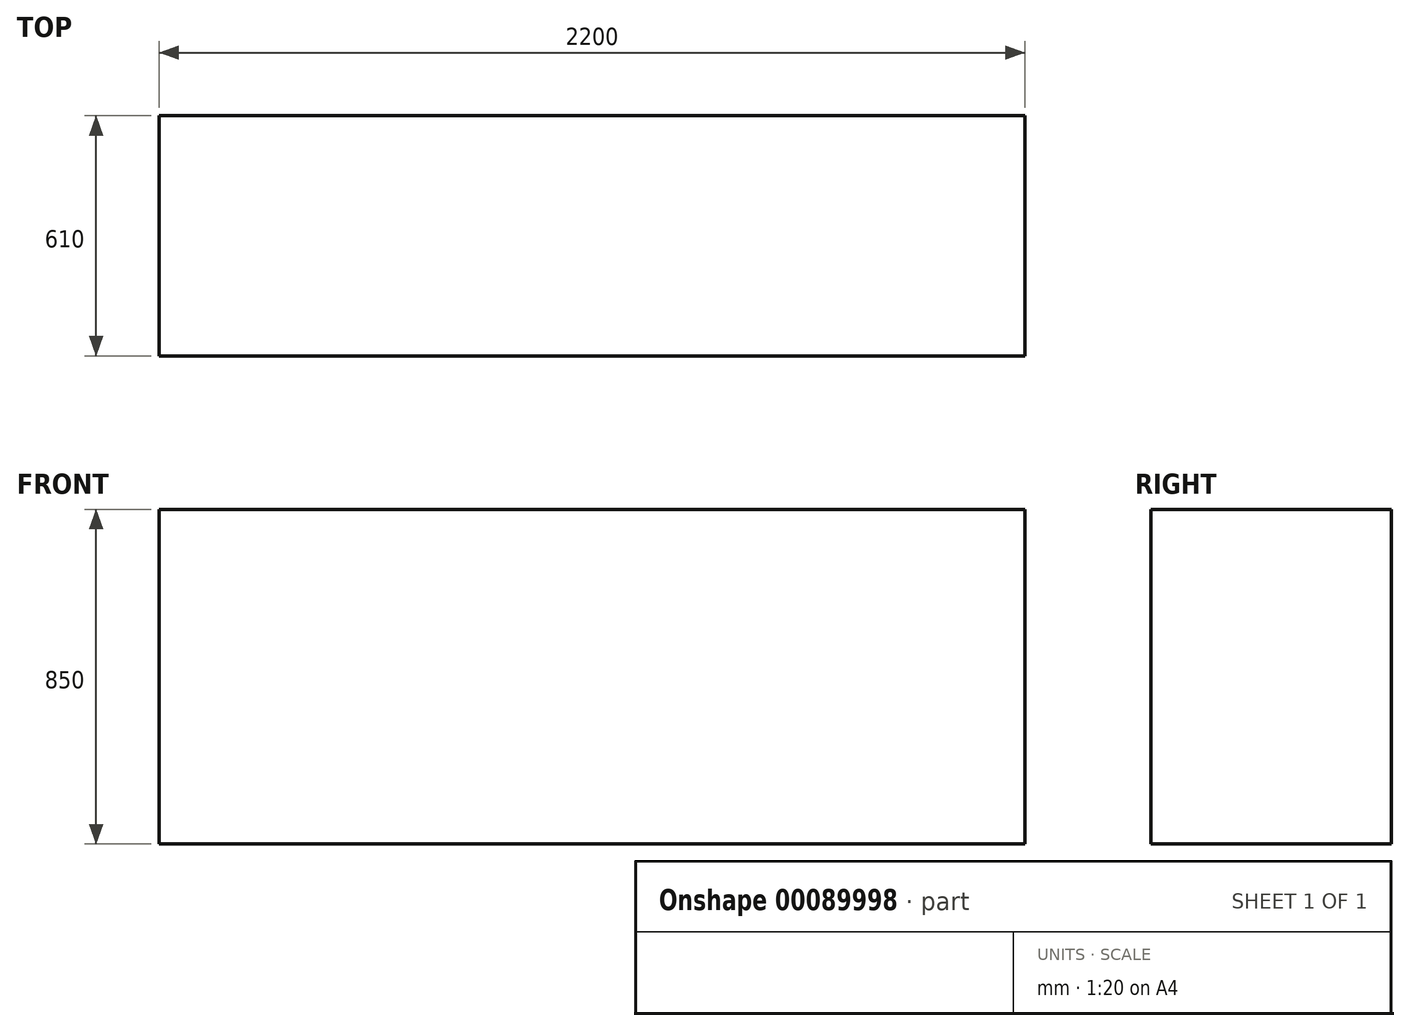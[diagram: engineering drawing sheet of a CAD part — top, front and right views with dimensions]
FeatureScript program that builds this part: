
annotation { "Feature Type Name" : "Feature", "Feature Type Description" : "" }
export const myFeature = defineFeature(function(context is Context, id is Id, definition is map)
    precondition{}
    {
        {
            var Q0;
            Q0=qCreatedBy(makeId("Top.planeOp"),FACE);
            var sketch = newSketch(context, id + "F0", { "sketchPlane" : qUnion([Q0])});
            skLineSegment(sketch, "E0.bottom", {"start": v(0, 0) * mm, "end": v(2200, 0) * mm});
            skLineSegment(sketch, "E0.top", {"start": v(0, 610) * mm, "end": v(2200, 610) * mm});
            skLineSegment(sketch, "E0.left", {"start": v(0, 0) * mm, "end": v(0, 610) * mm});
            skLineSegment(sketch, "E0.right", {"start": v(2200, 0) * mm, "end": v(2200, 610) * mm});
            skSolve(sketch);
        }
        {
            var Q0;
            Q0 = qSketchRegion(id + "F0", true);
            extrude(context, id + "F1", {"entities" : qUnion([Q0]), "depth" : 850 * mm});
        }
    });
